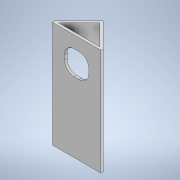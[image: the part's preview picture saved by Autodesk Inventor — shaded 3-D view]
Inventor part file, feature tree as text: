
AUTODESK INVENTOR PART (.ipt)
format: ipt  version: 2020 (Build 240168000, 168)  size: 137,728 bytes
history: native  units: mm
features: extrude x3, sketch x3
ambient origin geometry x8: Origin, YZ Plane, XZ Plane, XY Plane, X Axis, Y Axis, Z Axis, Center Point
bodies: Solid1 (feature_tree)
feature tree (6):
  extrude  "Extrusion1"  Depth=220.0mm
  extrude  "Extrusion2"  TaperAngle=45.0deg  [1 undecoded]
  extrude  "Extrusion5"  Depth=5.0mm
  sketch  "Sketch1"  dims[d0=100.0mm d1=220.0mm]
  sketch  "Sketch2"  dims[d2=5.0mm d3=0.0mm d4=45.0deg]
  sketch  "Sketch5"  dims[d5=5.0mm d6=5.0mm d7=45.0mm d8=0.0mm d16=50.0mm d17=50.0mm d18=20.0mm d19=5.0mm d20=0.0mm]
note: 1 required parameter value undecoded (feature->parameter linkage not recoverable at this tier; creation-order binding heuristic only, values carry confidence <= 0.55)
